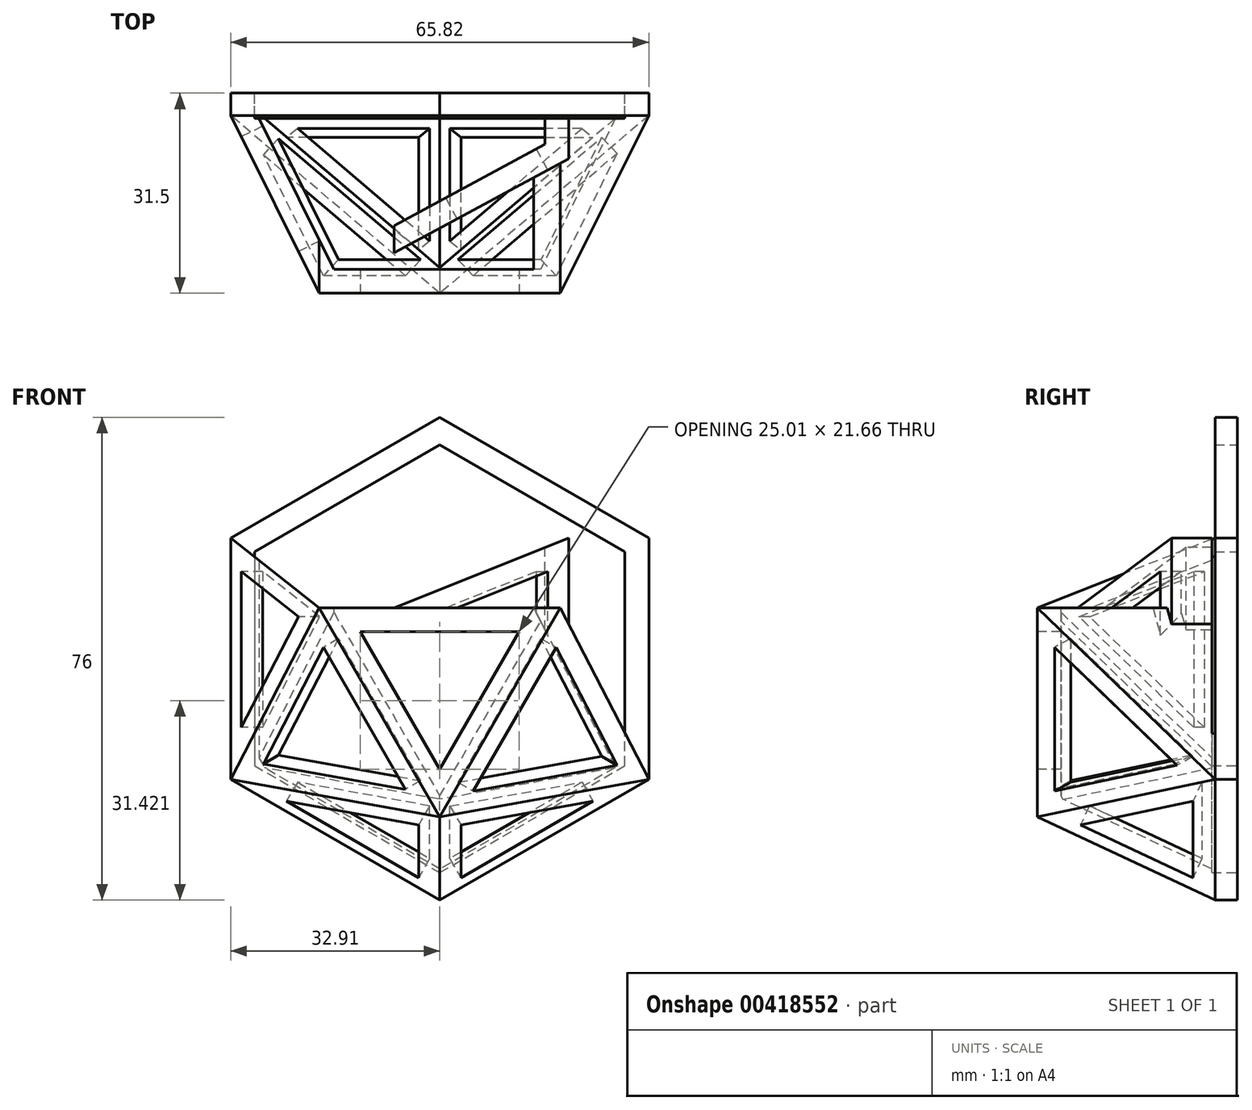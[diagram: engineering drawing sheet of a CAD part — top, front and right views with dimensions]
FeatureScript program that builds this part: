
annotation { "Feature Type Name" : "Feature", "Feature Type Description" : "" }
export const myFeature = defineFeature(function(context is Context, id is Id, definition is map)
    precondition{}
    {
        {
            var Q0;
            Q0=qCreatedBy(makeId("Front.planeOp"),FACE);
            var sketch = newSketch(context, id + "F0", { "sketchPlane" : qUnion([Q0])});
            skCircle(sketch, "E0.cCircle", {"center": v(0, 0) * mm, "radius": 38 * mm, "construction": true});
            skLineSegment(sketch, "E0.0", {"start": v(-32.9, 19) * mm, "end": v(0, 38) * mm});
            skLineSegment(sketch, "E0.1", {"start": v(0, 38) * mm, "end": v(32.9, 19) * mm});
            skLineSegment(sketch, "E0.2", {"start": v(32.9, 19) * mm, "end": v(32.9, -19) * mm});
            skLineSegment(sketch, "E0.3", {"start": v(32.9, -19) * mm, "end": v(0, -38) * mm});
            skLineSegment(sketch, "E0.4", {"start": v(0, -38) * mm, "end": v(-32.9, -19) * mm});
            skLineSegment(sketch, "E0.5", {"start": v(-32.9, -19) * mm, "end": v(-32.9, 19) * mm});
            skSolve(sketch);
        }
        {
            var Q0;
            Q0=qCreatedBy(makeId("Front.planeOp"),FACE);
            cPlane(context, id + "F1", {"entities" : qUnion([Q0]), "cplaneType" : CPlaneType.OFFSET, "offset" : 28 * mm, "width" : 150 * mm, "height" : 150 * mm});
        }
        {
            var Q0;
            Q0=qCreatedBy(id+"F1.planeOp",FACE);
            var sketch = newSketch(context, id + "F2", { "sketchPlane" : qUnion([Q0])});
            skLineSegment(sketch, "E1", {"start": v(-19, 8) * mm, "end": v(0, -24.9) * mm});
            skLineSegment(sketch, "E2", {"start": v(0, -24.9) * mm, "end": v(19, 8) * mm});
            skLineSegment(sketch, "E3", {"start": v(19, 8) * mm, "end": v(-19, 8) * mm});
            skSolve(sketch);
        }
        {
            var Q0;
            Q0=sQuery(id+"F2.wireOp",VERTEX,"E3.end");
            var Q1;
            Q1=sQuery(id+"F2.wireOp",VERTEX,"E2.start");
            var Q2;
            Q2=sQuery(id+"F0.wireOp",VERTEX,"E0.5.start");
            cPlane(context, id + "F3", {"entities" : qUnion([Q0, Q1, Q2]), "cplaneType" : CPlaneType.THREE_POINT, "offset" : 25 * mm, "width" : 150 * mm, "height" : 150 * mm});
        }
        {
            var Q0;
            Q0=qCreatedBy(id+"F3.planeOp",FACE);
            var sketch = newSketch(context, id + "F4", { "sketchPlane" : qUnion([Q0])});
            skLineSegment(sketch, "E4", {"start": v(23.37, -8.39) * mm, "end": v(-19.45, -16.66) * mm});
            skLineSegment(sketch, "E5", {"start": v(-19.45, -16.66) * mm, "end": v(-1.35, 20.47) * mm});
            skLineSegment(sketch, "E6", {"start": v(-1.35, 20.47) * mm, "end": v(23.37, -8.39) * mm});
            skSolve(sketch);
        }
        {
            var Q0;
            Q0=sQuery(id+"F0.wireOp",VERTEX,"E0.5.start");
            var Q1;
            Q1=sQuery(id+"F0.wireOp",VERTEX,"E0.5.end");
            var Q2;
            Q2=sQuery(id+"F2.wireOp",VERTEX,"E3.end");
            cPlane(context, id + "F5", {"entities" : qUnion([Q0, Q1, Q2]), "cplaneType" : CPlaneType.THREE_POINT, "offset" : 25 * mm, "width" : 150 * mm, "height" : 150 * mm});
        }
        {
            var Q0;
            Q0=qCreatedBy(id+"F5.planeOp",FACE);
            var sketch = newSketch(context, id + "F6", { "sketchPlane" : qUnion([Q0])});
            skLineSegment(sketch, "E7", {"start": v(16.62, 8) * mm, "end": v(-14.64, -19) * mm});
            skLineSegment(sketch, "E8", {"start": v(-14.64, -19) * mm, "end": v(-14.64, 19) * mm});
            skLineSegment(sketch, "E9", {"start": v(-14.64, 19) * mm, "end": v(16.62, 8) * mm});
            skSolve(sketch);
        }
        {
            var Q0;
            Q0=sQuery(id+"F2.wireOp",VERTEX,"E2.start");
            var Q1;
            Q1=sQuery(id+"F6.wireOp",VERTEX,"E8.start");
            var Q2;
            Q2=sQuery(id+"F0.wireOp",VERTEX,"E0.4.start");
            cPlane(context, id + "F7", {"entities" : qUnion([Q0, Q1, Q2]), "cplaneType" : CPlaneType.THREE_POINT, "offset" : 25 * mm, "width" : 150 * mm, "height" : 150 * mm});
        }
        {
            var Q0;
            Q0=qCreatedBy(id+"F7.planeOp",FACE);
            var sketch = newSketch(context, id + "F8", { "sketchPlane" : qUnion([Q0])});
            skLineSegment(sketch, "E10", {"start": v(15.95, -14.81) * mm, "end": v(-21.18, 8.05) * mm});
            skLineSegment(sketch, "E11", {"start": v(-21.18, 8.05) * mm, "end": v(15.95, 16.1) * mm});
            skLineSegment(sketch, "E12", {"start": v(15.95, 16.1) * mm, "end": v(15.95, -14.81) * mm});
            skSolve(sketch);
        }
        {
            var Q0;
            Q0=sQuery(id+"F8.wireOp",VERTEX,"E12.end");
            var Q1;
            Q1=sQuery(id+"F8.wireOp",VERTEX,"E12.start");
            var Q2;
            Q2=sQuery(id+"F0.wireOp",VERTEX,"E0.3.start");
            cPlane(context, id + "F9", {"entities" : qUnion([Q0, Q1, Q2]), "cplaneType" : CPlaneType.THREE_POINT, "offset" : 25 * mm, "width" : 150 * mm, "height" : 150 * mm});
        }
        {
            var Q0;
            Q0=qCreatedBy(id+"F9.planeOp",FACE);
            var sketch = newSketch(context, id + "F10", { "sketchPlane" : qUnion([Q0])});
            skLineSegment(sketch, "E13", {"start": v(-15.95, -14.81) * mm, "end": v(-15.95, 16.1) * mm});
            skLineSegment(sketch, "E14", {"start": v(-15.95, 16.1) * mm, "end": v(21.18, 8.05) * mm});
            skLineSegment(sketch, "E15", {"start": v(21.18, 8.05) * mm, "end": v(-15.95, -14.81) * mm});
            skSolve(sketch);
        }
        {
            var Q0;
            Q0=sQuery(id+"F10.wireOp",VERTEX,"E13.start");
            var Q1;
            Q1=sQuery(id+"F2.wireOp",VERTEX,"E3.start");
            var Q2;
            Q2=sQuery(id+"F10.wireOp",VERTEX,"E15.start");
            cPlane(context, id + "F11", {"entities" : qUnion([Q0, Q1, Q2]), "cplaneType" : CPlaneType.THREE_POINT, "offset" : 25 * mm, "width" : 150 * mm, "height" : 150 * mm});
        }
        {
            var Q0;
            Q0=qCreatedBy(id+"F11.planeOp",FACE);
            var sketch = newSketch(context, id + "F12", { "sketchPlane" : qUnion([Q0])});
            skLineSegment(sketch, "E16", {"start": v(-23.37, -8.39) * mm, "end": v(19.45, -16.66) * mm});
            skLineSegment(sketch, "E17", {"start": v(19.45, -16.66) * mm, "end": v(1.35, 20.47) * mm});
            skLineSegment(sketch, "E18", {"start": v(1.35, 20.47) * mm, "end": v(-23.37, -8.39) * mm});
            skSolve(sketch);
        }
        {
            var Q0;
            Q0=sQuery(id+"F0.wireOp",VERTEX,"E0.1.start");
            var Q1;
            Q1=sQuery(id+"F6.wireOp",VERTEX,"E9.end");
            var Q2;
            Q2=sQuery(id+"F6.wireOp",VERTEX,"E9.start");
            cPlane(context, id + "F13", {"entities" : qUnion([Q0, Q1, Q2]), "cplaneType" : CPlaneType.THREE_POINT, "offset" : 25 * mm, "width" : 150 * mm, "height" : 150 * mm});
        }
        {
            var Q0;
            Q0=qCreatedBy(id+"F13.planeOp",FACE);
            var sketch = newSketch(context, id + "F14", { "sketchPlane" : qUnion([Q0])});
            skLineSegment(sketch, "E19", {"start": v(-7.51, -18.66) * mm, "end": v(13.54, 21.36) * mm});
            skLineSegment(sketch, "E20", {"start": v(13.54, 21.36) * mm, "end": v(-22.93, 10.68) * mm});
            skLineSegment(sketch, "E21", {"start": v(-22.93, 10.68) * mm, "end": v(-7.51, -18.66) * mm});
            skSolve(sketch);
        }
        {
            var Q0;
            Q0=sQuery(id+"F12.wireOp",VERTEX,"E17.end");
            var Q1;
            Q1=sQuery(id+"F14.wireOp",VERTEX,"E20.start");
            var Q2;
            Q2=sQuery(id+"F14.wireOp",VERTEX,"E21.end");
            cPlane(context, id + "F15", {"entities" : qUnion([Q0, Q1, Q2]), "cplaneType" : CPlaneType.THREE_POINT, "offset" : 25 * mm, "width" : 150 * mm, "height" : 150 * mm});
        }
        {
            var Q0;
            Q0=qCreatedBy(id+"F15.planeOp",FACE);
            var sketch = newSketch(context, id + "F16", { "sketchPlane" : qUnion([Q0])});
            skLineSegment(sketch, "E22", {"start": v(19, -13.26) * mm, "end": v(0, 27.78) * mm});
            skLineSegment(sketch, "E23", {"start": v(0, 27.78) * mm, "end": v(-19, -13.26) * mm});
            skLineSegment(sketch, "E24", {"start": v(19, -13.26) * mm, "end": v(-19, -13.26) * mm});
            skSolve(sketch);
        }
        {
            var Q0;
            Q0=sQuery(id+"F0.wireOp",VERTEX,"E0.2.start");
            var Q1;
            Q1=sQuery(id+"F12.wireOp",VERTEX,"E17.start");
            var Q2;
            Q2=sQuery(id+"F16.wireOp",VERTEX,"E24.start");
            cPlane(context, id + "F17", {"entities" : qUnion([Q0, Q1, Q2]), "cplaneType" : CPlaneType.THREE_POINT, "offset" : 25 * mm, "width" : 150 * mm, "height" : 150 * mm});
        }
        {
            var Q0;
            Q0=qCreatedBy(id+"F17.planeOp",FACE);
            var sketch = newSketch(context, id + "F18", { "sketchPlane" : qUnion([Q0])});
            skLineSegment(sketch, "E25", {"start": v(-16.62, 8) * mm, "end": v(14.64, -19) * mm});
            skLineSegment(sketch, "E26", {"start": v(14.64, -19) * mm, "end": v(14.64, 19) * mm});
            skLineSegment(sketch, "E27", {"start": v(14.64, 19) * mm, "end": v(-16.62, 8) * mm});
            skSolve(sketch);
        }
        {
            var Q0;
            Q0=sQuery(id+"F18.wireOp",VERTEX,"E25.start");
            var Q1;
            Q1=sQuery(id+"F18.wireOp",VERTEX,"E27.start");
            var Q2;
            Q2=sQuery(id+"F16.wireOp",VERTEX,"E23.start");
            cPlane(context, id + "F19", {"entities" : qUnion([Q0, Q1, Q2]), "cplaneType" : CPlaneType.THREE_POINT, "offset" : 25 * mm, "width" : 150 * mm, "height" : 150 * mm});
        }
        {
            var Q0;
            Q0 = qSketchRegion(id + "F0", true);
            extrude(context, id + "F20", {"entities" : qUnion([Q0]), "oppositeDirection" : true, "depth" : 3.5 * mm});
        }
        {
            var Q0;
            Q0=makeQuery(id+"F2.imprint","IMPRINT",FACE,{"disambiguationData":[TD([[makeQuery(id+"F2.imprint","IMPRINT",EDGE,{"derivedFrom":sQuery(id+"F2.wireOp",EDGE,"E1")}),1.0]])]});
            var Q1;
            Q1=makeQuery(id+"F6.imprint","IMPRINT",FACE,{"disambiguationData":[TD([[makeQuery(id+"F6.imprint","IMPRINT",EDGE,{"derivedFrom":sQuery(id+"F6.wireOp",EDGE,"E7")}),-1.0]])]});
            var Q2;
            Q2=makeQuery(id+"F4.imprint","IMPRINT",FACE,{"disambiguationData":[TD([[makeQuery(id+"F4.imprint","IMPRINT",EDGE,{"derivedFrom":sQuery(id+"F4.wireOp",EDGE,"E4")}),-1.0]])]});
            var Q3;
            Q3=makeQuery(id+"F8.imprint","IMPRINT",FACE,{"disambiguationData":[TD([[makeQuery(id+"F8.imprint","IMPRINT",EDGE,{"derivedFrom":sQuery(id+"F8.wireOp",EDGE,"E10")}),-1.0]])]});
            var Q4;
            Q4=makeQuery(id+"F10.imprint","IMPRINT",FACE,{"disambiguationData":[TD([[makeQuery(id+"F10.imprint","IMPRINT",EDGE,{"derivedFrom":sQuery(id+"F10.wireOp",EDGE,"E13")}),-1.0]])]});
            var Q5;
            Q5=makeQuery(id+"F12.imprint","IMPRINT",FACE,{"disambiguationData":[TD([[makeQuery(id+"F12.imprint","IMPRINT",EDGE,{"derivedFrom":sQuery(id+"F12.wireOp",EDGE,"E16")}),1.0]])]});
            var Q6;
            Q6=makeQuery(id+"F18.imprint","IMPRINT",FACE,{"disambiguationData":[TD([[makeQuery(id+"F18.imprint","IMPRINT",EDGE,{"derivedFrom":sQuery(id+"F18.wireOp",EDGE,"E25")}),1.0]])]});
            var Q7;
            Q7=makeQuery(id+"F20.opExtrude","CAP_FACE",FACE,{"disambiguationData":[OSD([sQuery(id+"F0.wireOp",EDGE,"E0.0"),sQuery(id+"F0.wireOp",EDGE,"E0.1"),sQuery(id+"F0.wireOp",EDGE,"E0.2"),sQuery(id+"F0.wireOp",EDGE,"E0.3"),sQuery(id+"F0.wireOp",EDGE,"E0.4"),sQuery(id+"F0.wireOp",EDGE,"E0.5")])],"isStart":true});
            extrude(context, id + "F21", {"entities" : qUnion([Q0, Q1, Q2, Q3, Q4, Q5, Q6]), "operationType" : NewBodyOperationType.ADD, "endBound" : BoundingType.UP_TO_SURFACE, "oppositeDirection" : true, "endBoundEntityFace" : qUnion([Q7]), "depth" : 25 * mm});
        }
        {
            var Q0;
            Q0=makeQuery(id+"F21.opExtrude","SWEPT_FACE",FACE,{"disambiguationData":[OSD([sQuery(id+"F2.wireOp",EDGE,"E3")])]});
            var Q1;
            Q1=makeQuery(id+"F21.opExtrude","SWEPT_FACE",FACE,{"disambiguationData":[OSD([sQuery(id+"F18.wireOp",EDGE,"E27")])]});
            var Q2;
            Q2=makeQuery(id+"F21.opExtrude","SWEPT_FACE",FACE,{"disambiguationData":[OSD([sQuery(id+"F6.wireOp",EDGE,"E9")])]});
            var Q3;
            Q3=makeQuery(id+"F21.opExtrude","SWEPT_FACE",FACE,{"disambiguationData":[OSD([sQuery(id+"F2.wireOp",EDGE,"WbOHPHKK-Nw33-ZnTN-OlqM-fbYxj0YIFz8h")])]});
            var Q4;
            Q4=makeQuery(id+"F21.opExtrude","SWEPT_FACE",FACE,{"disambiguationData":[OSD([sQuery(id+"F2.wireOp",EDGE,"5qjFDsdd-swa0-z9kg-JQke-vFuo6n7Ob3zi")])]});
            var Q5;
            Q5=makeQuery(id+"F21.opExtrude","SWEPT_FACE",FACE,{"disambiguationData":[OSD([sQuery(id+"F2.wireOp",EDGE,"GYQIImPS-komu-qjez-Sc8f-C5i2az53FD9t")])]});
            shell(context, id + "F22", {"entities" : qUnion([Q0, Q1, Q2, Q3, Q4, Q5]), "thickness" : 3.75 * mm});
        }
        {
            var Q0;
            Q0=makeQuery(id+"F21.opExtrude","CAP_FACE",FACE,{"disambiguationData":[OSD([sQuery(id+"F2.wireOp",EDGE,"E1"),sQuery(id+"F2.wireOp",EDGE,"E2"),sQuery(id+"F2.wireOp",EDGE,"E3")])],"isStart":true});
            var sketch = newSketch(context, id + "F23", { "sketchPlane" : qUnion([Q0])});
            skLineSegment(sketch, "E28", {"start": v(-12.5, 4.25) * mm, "end": v(12.5, 4.25) * mm});
            skLineSegment(sketch, "E29", {"start": v(12.5, 4.25) * mm, "end": v(0, -17.4) * mm});
            skLineSegment(sketch, "E30", {"start": v(0, -17.4) * mm, "end": v(-12.5, 4.25) * mm});
            skSolve(sketch);
        }
        {
            var Q0;
            Q0 = qSketchRegion(id + "F23", true);
            extrude(context, id + "F24", {"entities" : qUnion([Q0]), "operationType" : NewBodyOperationType.REMOVE, "oppositeDirection" : true, "depth" : 6 * mm});
        }
        {
            var Q0;
            Q0=makeQuery(id+"F21.opExtrude","CAP_FACE",FACE,{"disambiguationData":[OSD([sQuery(id+"F4.wireOp",EDGE,"E4"),sQuery(id+"F4.wireOp",EDGE,"E5"),sQuery(id+"F4.wireOp",EDGE,"E6")])],"isStart":false});
            var sketch = newSketch(context, id + "F25", { "sketchPlane" : qUnion([Q0])});
            skLineSegment(sketch, "E31", {"start": v(-0.48, 13.7) * mm, "end": v(-12.8, -11.56) * mm});
            skLineSegment(sketch, "E32", {"start": v(-12.8, -11.56) * mm, "end": v(16.32, -5.93) * mm});
            skLineSegment(sketch, "E33", {"start": v(16.32, -5.93) * mm, "end": v(-0.48, 13.7) * mm});
            skSolve(sketch);
        }
        {
            var Q0;
            Q0 = qSketchRegion(id + "F25", true);
            extrude(context, id + "F26", {"entities" : qUnion([Q0]), "operationType" : NewBodyOperationType.REMOVE, "oppositeDirection" : true, "depth" : 6 * mm});
        }
        {
            var Q0;
            Q0=makeQuery(id+"F21.opExtrude","CAP_FACE",FACE,{"disambiguationData":[OSD([sQuery(id+"F12.wireOp",EDGE,"E16"),sQuery(id+"F12.wireOp",EDGE,"E17"),sQuery(id+"F12.wireOp",EDGE,"E18")])],"isStart":false});
            var sketch = newSketch(context, id + "F27", { "sketchPlane" : qUnion([Q0])});
            skLineSegment(sketch, "E34", {"start": v(-16.51, -6.15) * mm, "end": v(12.93, -11.84) * mm});
            skLineSegment(sketch, "E35", {"start": v(12.93, -11.84) * mm, "end": v(0.48, 13.7) * mm});
            skLineSegment(sketch, "E36", {"start": v(0.48, 13.7) * mm, "end": v(-16.51, -6.15) * mm});
            skSolve(sketch);
        }
        {
            var Q0;
            Q0 = qSketchRegion(id + "F27", true);
            extrude(context, id + "F28", {"entities" : qUnion([Q0]), "operationType" : NewBodyOperationType.REMOVE, "oppositeDirection" : true, "depth" : 6 * mm});
        }
        {
            var Q0;
            Q0=makeQuery(id+"F21.opExtrude","CAP_FACE",FACE,{"disambiguationData":[OSD([sQuery(id+"F18.wireOp",EDGE,"E25"),sQuery(id+"F18.wireOp",EDGE,"E26"),sQuery(id+"F18.wireOp",EDGE,"E27")])],"isStart":false});
            var sketch = newSketch(context, id + "F29", { "sketchPlane" : qUnion([Q0])});
            skLineSegment(sketch, "E37", {"start": v(-9.28, 6.6) * mm, "end": v(10.9, -10.8) * mm});
            skLineSegment(sketch, "E38", {"start": v(10.9, -10.8) * mm, "end": v(10.9, 13.7) * mm});
            skLineSegment(sketch, "E39", {"start": v(10.9, 13.7) * mm, "end": v(-9.28, 6.6) * mm});
            skSolve(sketch);
        }
        {
            var Q0;
            Q0 = qSketchRegion(id + "F29", true);
            extrude(context, id + "F30", {"entities" : qUnion([Q0]), "operationType" : NewBodyOperationType.REMOVE, "oppositeDirection" : true, "depth" : 6 * mm});
        }
        {
            var Q0;
            Q0=makeQuery(id+"F21.opExtrude","CAP_FACE",FACE,{"disambiguationData":[OSD([sQuery(id+"F6.wireOp",EDGE,"E7"),sQuery(id+"F6.wireOp",EDGE,"E8"),sQuery(id+"F6.wireOp",EDGE,"E9")])],"isStart":false});
            var sketch = newSketch(context, id + "F31", { "sketchPlane" : qUnion([Q0])});
            skLineSegment(sketch, "E40", {"start": v(9.28, 6.6) * mm, "end": v(-10.9, 13.7) * mm});
            skLineSegment(sketch, "E41", {"start": v(-10.9, 13.7) * mm, "end": v(-10.9, -10.8) * mm});
            skLineSegment(sketch, "E42", {"start": v(-10.9, -10.8) * mm, "end": v(9.28, 6.6) * mm});
            skSolve(sketch);
        }
        {
            var Q0;
            Q0 = qSketchRegion(id + "F31", true);
            extrude(context, id + "F32", {"entities" : qUnion([Q0]), "operationType" : NewBodyOperationType.REMOVE, "oppositeDirection" : true, "depth" : 6 * mm});
        }
        {
            var Q0;
            Q0=makeQuery(id+"F20.opExtrude","CAP_FACE",FACE,{"disambiguationData":[OSD([sQuery(id+"F0.wireOp",EDGE,"E0.0"),sQuery(id+"F0.wireOp",EDGE,"E0.1"),sQuery(id+"F0.wireOp",EDGE,"E0.2"),sQuery(id+"F0.wireOp",EDGE,"E0.3"),sQuery(id+"F0.wireOp",EDGE,"E0.4"),sQuery(id+"F0.wireOp",EDGE,"E0.5")])],"isStart":false});
            var sketch = newSketch(context, id + "F33", { "sketchPlane" : qUnion([Q0])});
            skCircle(sketch, "E43.cCircle", {"center": v(0, 0) * mm, "radius": 33.67 * mm, "construction": true});
            skLineSegment(sketch, "E43.0", {"start": v(29.16, 16.83) * mm, "end": v(29.16, -16.83) * mm});
            skLineSegment(sketch, "E43.1", {"start": v(29.16, -16.83) * mm, "end": v(0, -33.67) * mm});
            skLineSegment(sketch, "E43.2", {"start": v(0, -33.67) * mm, "end": v(-29.16, -16.83) * mm});
            skLineSegment(sketch, "E43.3", {"start": v(-29.16, -16.83) * mm, "end": v(-29.16, 16.83) * mm});
            skLineSegment(sketch, "E43.4", {"start": v(-29.16, 16.83) * mm, "end": v(0, 33.67) * mm});
            skLineSegment(sketch, "E43.5", {"start": v(0, 33.67) * mm, "end": v(29.16, 16.83) * mm});
            skLineSegment(sketch, "E44", {"start": v(0, 0) * mm, "end": v(0, 56.45) * mm, "construction": true});
            skSolve(sketch);
        }
        {
            var Q0;
            Q0 = qSketchRegion(id + "F33", true);
            extrude(context, id + "F34", {"entities" : qUnion([Q0]), "operationType" : NewBodyOperationType.REMOVE, "oppositeDirection" : true, "depth" : 4 * mm});
        }
        {
            var Q0;
            Q0=makeQuery(id+"F21.opExtrude","CAP_FACE",FACE,{"disambiguationData":[OSD([sQuery(id+"F8.wireOp",EDGE,"E10"),sQuery(id+"F8.wireOp",EDGE,"E11"),sQuery(id+"F8.wireOp",EDGE,"E12")])],"isStart":false});
            var sketch = newSketch(context, id + "F35", { "sketchPlane" : qUnion([Q0])});
            skLineSegment(sketch, "E45", {"start": v(-11.28, -6.36) * mm, "end": v(12.2, 8.1) * mm});
            skLineSegment(sketch, "E46", {"start": v(12.2, 8.1) * mm, "end": v(12.2, -11.44) * mm});
            skLineSegment(sketch, "E47", {"start": v(12.2, -11.44) * mm, "end": v(-11.28, -6.36) * mm});
            skSolve(sketch);
        }
        {
            var Q0;
            Q0 = qSketchRegion(id + "F35", true);
            extrude(context, id + "F36", {"entities" : qUnion([Q0]), "operationType" : NewBodyOperationType.REMOVE, "oppositeDirection" : true, "depth" : 6 * mm});
        }
        {
            var Q0;
            Q0=makeQuery(id+"F21.opExtrude","CAP_FACE",FACE,{"disambiguationData":[OSD([sQuery(id+"F10.wireOp",EDGE,"E13"),sQuery(id+"F10.wireOp",EDGE,"E14"),sQuery(id+"F10.wireOp",EDGE,"E15")])],"isStart":false});
            var sketch = newSketch(context, id + "F37", { "sketchPlane" : qUnion([Q0])});
            skLineSegment(sketch, "E48", {"start": v(-12.2, 8.1) * mm, "end": v(-12.2, -11.44) * mm});
            skLineSegment(sketch, "E49", {"start": v(-12.2, -11.44) * mm, "end": v(11.28, -6.36) * mm});
            skLineSegment(sketch, "E50", {"start": v(11.28, -6.36) * mm, "end": v(-12.2, 8.1) * mm});
            skSolve(sketch);
        }
        {
            var Q0;
            Q0 = qSketchRegion(id + "F37", true);
            extrude(context, id + "F38", {"entities" : qUnion([Q0]), "operationType" : NewBodyOperationType.REMOVE, "oppositeDirection" : true, "depth" : 6 * mm});
        }
    });
